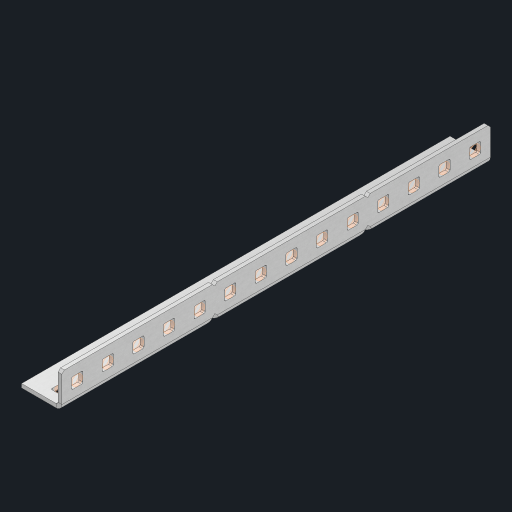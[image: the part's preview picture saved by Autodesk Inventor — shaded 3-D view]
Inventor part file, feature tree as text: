
AUTODESK INVENTOR PART (.ipt)
format: ipt  version: 2023 (Build 270158000, 158)  size: 653,312 bytes
history: native  units: in
note: dims shown in document units (in); Inventor stores cm internally (conversion verified against a paired STEP export)
features: other x33, extrude x27, sheet_metal_op x10, sketch x8, mirror x1, pattern_linear x1, chamfer x1
ambient origin geometry x8: Origin, YZ Plane, XZ Plane, XY Plane, X Axis, Y Axis, Z Axis, Center Point
bodies: Solid1 (feature_tree), Body (feature_tree)
feature tree (81):
  other  "Flange Pattern Plane"
  sheet_metal_op  "Flange Pattern"
  sheet_metal_op  "Body Pattern"
  other  "Arc Length"
  mirror  "Notch Mirror"
  pattern_linear  "Notch Pattern"  Spacing1=0.25in  [1 undecoded]
  chamfer  "End Chamfer"
  extrude  "Half Cut"  Depth=0.0625in
  sketch  "Sketch1"  dims[d0=1.5in]
  other  "Plate1"
  sketch  "Sketch2"  dims[d1=7.0in]
  other  "Plate2"
  sheet_metal_op  "Bend1"
  sheet_metal_op  "Corner1"
  sketch  "Sketch3"  dims[d2=0.0625in]
  other  "Flange Pattern Sketch"
  sketch  "Sketch7"  dims[d3=0.0625in]
  other  "Srf1"
  other  "Srf2"
  sketch  "Sketch8"  dims[d4=0.0312in]
  sketch  "Sketch9"  dims[d5=0.125in]
  other  "Srf91"
  sheet_metal_op  "Body Pattern Sketch"
  other  "Srf92"
  sketch  "Sketch13"  dims[d6=0.0625in]
  sketch  "Sketch14"  dims[d7=0.5in d8=90.0deg d9=0.0312in d10=0.25in d11=0.0625in d12=0.0625in d16=0.182in d17=0.02in d18=0.0625in d19=0.0in d20=0.25in d21=0.25in d46=0.172in d47=1.0in d48=0.0in d49=0.182in d50=0.02in d51=0.25in d52=0.25in d53=0.0625in d54=0.0in d55=0.172in d56=1.0in d57=0.0in d60=5.5118in d62=0.5in d63=0.3937in d65=0.5in d85=0.1473in d86=0.1782in d88=0.04in d89=0.0625in d90=0.0in d91=0.04in d92=0.0491in d95=2.5in d96=0.04in d97=0.25in d98=45.0deg d101=0.0in d102=2.497in d131=0.5in d132=5.5118in d134=0.5in d139=0.5in]
  other  "Srf856"
  other  "Srf1310"
  other  "Srf1311"
  other  "Srf1312"
  other  "Srf1376"
  other  "Srf1377"
  other  "Srf1728"
  other  "Srf1755"
  other  "Srf1878"
  other  "Srf1879"
  other  "Srf1880"
  other  "Srf1881"
  other  "Srf1882"
  other  "Srf1883"
  other  "Srf1884"
  other  "Srf1885"
  other  "Srf1942"
  other  "Srf1943"
  other  "Srf1944"
  other  "Srf1945"
  other  "Srf1946"
  other  "Srf1947"
  other  "Srf1948"
  other  "Srf1949"
  sheet_metal_op  "Flange Stamp"
  sheet_metal_op  "Flange Circle"
  sheet_metal_op  "Body Stamp"
  sheet_metal_op  "Body Circle"
  sheet_metal_op  "Notch"
  extrude  "ExtrusionSrf2"  Depth=0.0625in
  extrude  "ExtrusionSrf92"  Depth=0.5in
  extrude  "ExtrusionSrf856"  Depth=0.02in
  extrude  "ExtrusionSrf1310"  Depth=0.0625in
  extrude  "ExtrusionSrf1311"  TaperAngle=0.0deg  [1 undecoded]
  extrude  "ExtrusionSrf1312"  Depth=0.5in
  extrude  "ExtrusionSrf1376"  Depth=0.5in
  extrude  "ExtrusionSrf1377"  Depth=0.5in
  extrude  "ExtrusionSrf1728"  Depth=0.5in TaperAngle=0.0deg
  extrude  "ExtrusionSrf1755"  Depth=0.5in
  extrude  "ExtrusionSrf1878"  Depth=0.02in
  extrude  "ExtrusionSrf1879"  Depth=0.5in
  extrude  "ExtrusionSrf1880"  Depth=0.5in
  extrude  "ExtrusionSrf1881"  Depth=0.0625in
  extrude  "ExtrusionSrf1882"  TaperAngle=0.0deg  [1 undecoded]
  extrude  "ExtrusionSrf1883"  Depth=0.5in
  extrude  "ExtrusionSrf1884"  Depth=0.5in TaperAngle=0.0deg
  extrude  "ExtrusionSrf1885"  Depth=0.5in
  extrude  "ExtrusionSrf1942"  Depth=0.5in
  extrude  "ExtrusionSrf1943"  Depth=0.5in
  extrude  "ExtrusionSrf1944"  Depth=0.5in
  extrude  "ExtrusionSrf1945"  Depth=0.5in
  extrude  "ExtrusionSrf1946"  Depth=0.0625in
  extrude  "ExtrusionSrf1947"  TaperAngle=0.0deg  [1 undecoded]
  extrude  "ExtrusionSrf1948"  Depth=0.5in
  extrude  "ExtrusionSrf1949"  Depth=0.5in
note: 4 required parameter values undecoded (feature->parameter linkage not recoverable at this tier; creation-order binding heuristic only, values carry confidence <= 0.55)
